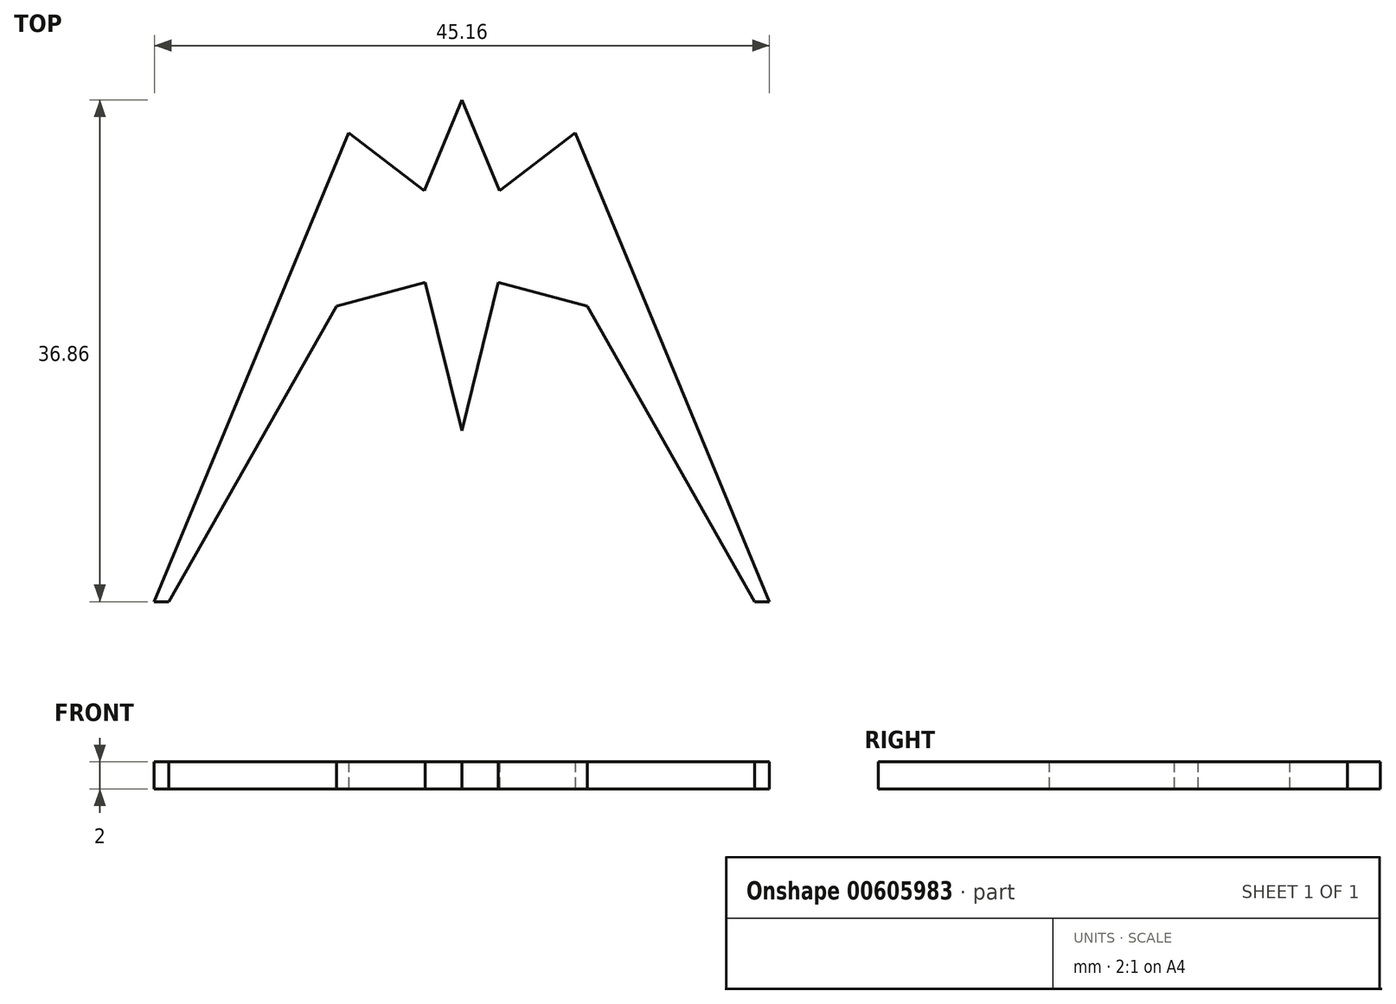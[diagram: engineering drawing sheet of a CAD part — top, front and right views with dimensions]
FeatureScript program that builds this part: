
annotation { "Feature Type Name" : "Feature", "Feature Type Description" : "" }
export const myFeature = defineFeature(function(context is Context, id is Id, definition is map)
    precondition{}
    {
        {
            var Q0;
            Q0=qCreatedBy(makeId("Top.planeOp"),FACE);
            var sketch = newSketch(context, id + "F0", { "sketchPlane" : qUnion([Q0])});
            skLineSegment(sketch, "E0", {"start": v(0, 14.35) * mm, "end": v(2.87, 7.42) * mm});
            skLineSegment(sketch, "E1", {"start": v(2.87, 7.42) * mm, "end": v(8.42, 11.68) * mm});
            skLineSegment(sketch, "E2", {"start": v(8.42, 11.68) * mm, "end": v(22.96, -23.41) * mm});
            skLineSegment(sketch, "E3", {"start": v(22.96, -23.41) * mm, "end": v(21.36, -23.41) * mm});
            skLineSegment(sketch, "E4", {"start": v(21.36, -23.41) * mm, "end": v(9.05, -1.65) * mm});
            skLineSegment(sketch, "E5", {"start": v(9.05, -1.65) * mm, "end": v(2.87, 0) * mm});
            skLineSegment(sketch, "E6", {"start": v(2.87, 0) * mm, "end": v(0, -11.65) * mm});
            skLineSegment(sketch, "E7", {"start": v(0, 14.35) * mm, "end": v(0, -11.65) * mm, "construction": true});
            skLineSegment(sketch, "E8.MirrorCS", {"start": v(0, 14.35) * mm, "end": v(-2.87, 7.42) * mm});
            skLineSegment(sketch, "E9.MirrorCS", {"start": v(-2.87, 7.42) * mm, "end": v(-8.42, 11.68) * mm});
            skLineSegment(sketch, "E10.MirrorCS", {"start": v(-8.42, 11.68) * mm, "end": v(-22.96, -23.41) * mm});
            skLineSegment(sketch, "E11.MirrorCS", {"start": v(-2.87, 0) * mm, "end": v(0, -11.65) * mm});
            skLineSegment(sketch, "E12.MirrorCS", {"start": v(-9.05, -1.65) * mm, "end": v(-2.87, 0) * mm});
            skLineSegment(sketch, "E13.MirrorCS", {"start": v(-21.36, -23.41) * mm, "end": v(-9.05, -1.65) * mm});
            skLineSegment(sketch, "E14.MirrorCS", {"start": v(-22.96, -23.41) * mm, "end": v(-21.36, -23.41) * mm});
            skLineSegment(sketch, "E15.0", {"start": v(0, 13.7) * mm, "end": v(-2.76, 7.02) * mm});
            skLineSegment(sketch, "E15.1", {"start": v(-2.76, 7.02) * mm, "end": v(-8.32, 11.28) * mm});
            skLineSegment(sketch, "E15.2", {"start": v(-8.32, 11.28) * mm, "end": v(-22.58, -23.16) * mm});
            skLineSegment(sketch, "E15.3", {"start": v(21.5, -23.16) * mm, "end": v(9.21, -1.44) * mm});
            skLineSegment(sketch, "E15.4", {"start": v(22.58, -23.16) * mm, "end": v(21.5, -23.16) * mm});
            skLineSegment(sketch, "E15.5", {"start": v(8.32, 11.28) * mm, "end": v(22.58, -23.16) * mm});
            skLineSegment(sketch, "E15.6", {"start": v(2.76, 7.02) * mm, "end": v(8.32, 11.28) * mm});
            skLineSegment(sketch, "E15.7", {"start": v(9.21, -1.44) * mm, "end": v(2.69, 0.3) * mm});
            skLineSegment(sketch, "E15.8", {"start": v(2.69, 0.3) * mm, "end": v(0, -10.6) * mm});
            skLineSegment(sketch, "E15.9", {"start": v(-2.69, 0.3) * mm, "end": v(0, -10.6) * mm});
            skLineSegment(sketch, "E15.10", {"start": v(0, 13.7) * mm, "end": v(2.76, 7.02) * mm});
            skLineSegment(sketch, "E15.11", {"start": v(-9.21, -1.44) * mm, "end": v(-2.69, 0.3) * mm});
            skLineSegment(sketch, "E15.12", {"start": v(-21.5, -23.16) * mm, "end": v(-9.21, -1.44) * mm});
            skLineSegment(sketch, "E15.13", {"start": v(-22.58, -23.16) * mm, "end": v(-21.5, -23.16) * mm});
            skSolve(sketch);
        }
        {
            var Q0;
            Q0=makeQuery(id+"F0.imprint","IMPRINT",FACE,{"disambiguationData":[TD([[makeQuery(id+"F0.imprint","IMPRINT",EDGE,{"derivedFrom":sQuery(id+"F0.wireOp",EDGE,"E15.0")}),1.0]])]});
            extrude(context, id + "F1", {"entities" : qUnion([Q0]), "depth" : 2 * mm});
        }
    });
